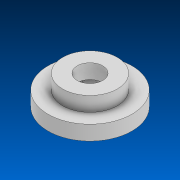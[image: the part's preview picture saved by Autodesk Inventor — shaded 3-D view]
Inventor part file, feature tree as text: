
AUTODESK INVENTOR PART (.ipt)
format: ipt  version: 2022 (Build 260153000, 153)  size: 114,688 bytes
history: native  units: in
note: dims shown in document units (in); Inventor stores cm internally (conversion verified against a paired STEP export)
features: sketch x2, revolve x1, extrude x1
ambient origin geometry x8: Origin, YZ Plane, XZ Plane, XY Plane, X Axis, Y Axis, Z Axis, Center Point
bodies: Solid1 (feature_tree)
feature tree (4):
  revolve  "Revolution1"  [1 undecoded]
  extrude  "Extrusion1"  Depth=0.1in
  sketch  "Sketch1"  dims[d0=0.0875in d1=0.1875in]
  sketch  "Sketch2"  dims[d2=0.1in d3=0.1in d4=0.1in d6=90.0deg d7=0.125in d8=0.25in d9=1.0in d10=0.0in]
note: 1 required parameter value undecoded (feature->parameter linkage not recoverable at this tier; creation-order binding heuristic only, values carry confidence <= 0.55)
